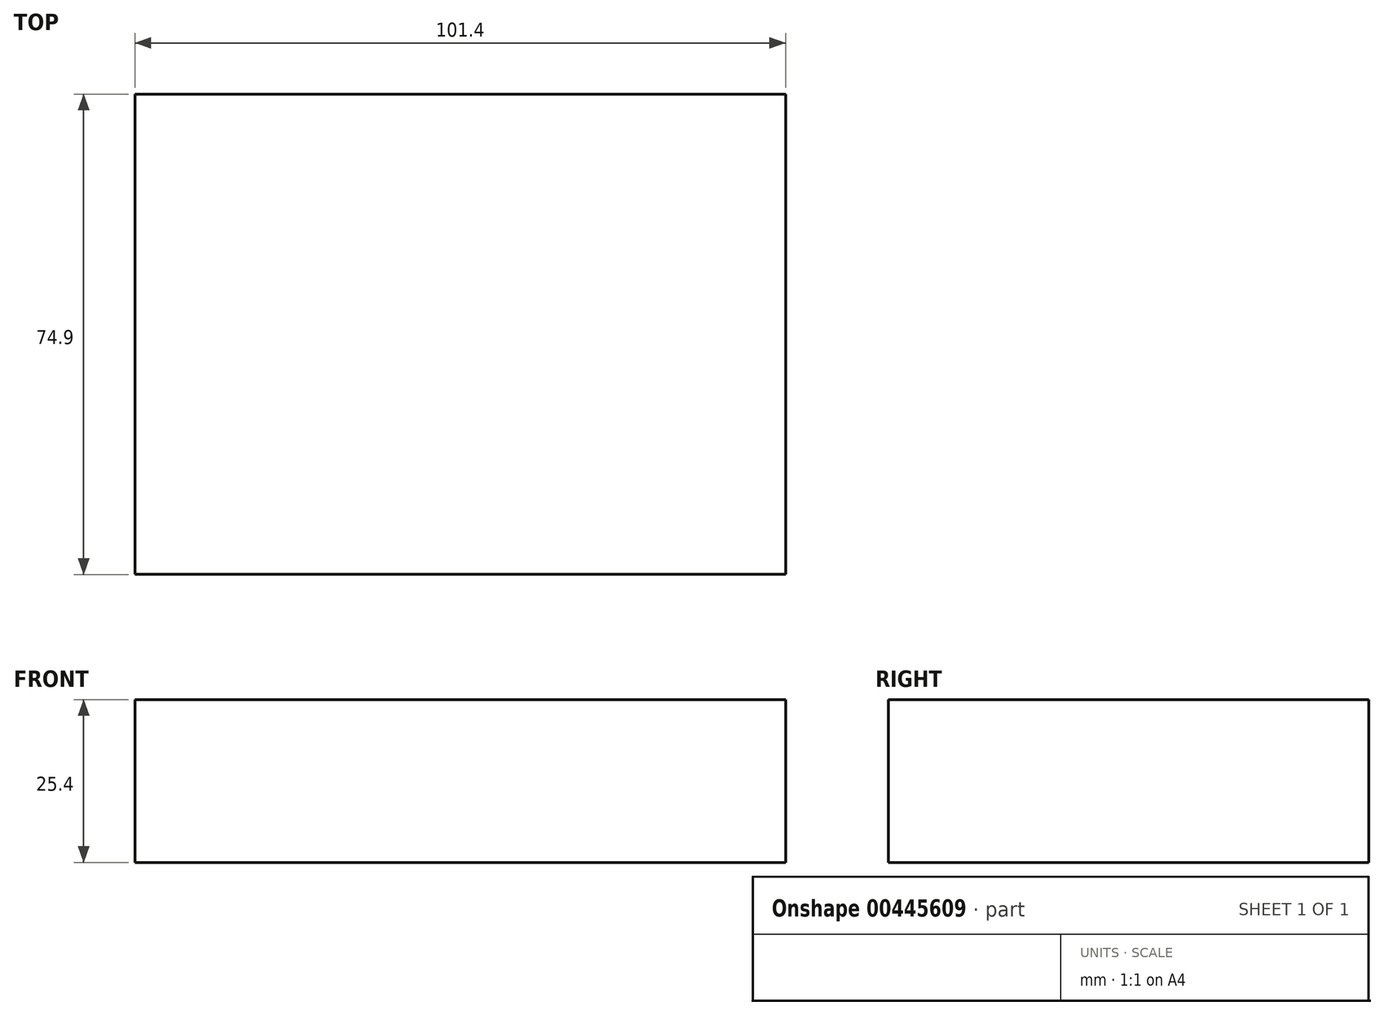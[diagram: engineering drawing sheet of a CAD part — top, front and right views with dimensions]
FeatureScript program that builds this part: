
annotation { "Feature Type Name" : "Feature", "Feature Type Description" : "" }
export const myFeature = defineFeature(function(context is Context, id is Id, definition is map)
    precondition{}
    {
        {
            var Q0;
            Q0=qCreatedBy(makeId("Top.planeOp"),FACE);
            var sketch = newSketch(context, id + "F0", { "sketchPlane" : qUnion([Q0])});
            skLineSegment(sketch, "E0.bottom", {"start": v(50.7, 37.45) * mm, "end": v(-50.7, 37.45) * mm});
            skLineSegment(sketch, "E0.top", {"start": v(50.7, -37.45) * mm, "end": v(-50.7, -37.45) * mm});
            skLineSegment(sketch, "E0.left", {"start": v(50.7, 37.45) * mm, "end": v(50.7, -37.45) * mm});
            skLineSegment(sketch, "E0.right", {"start": v(-50.7, 37.45) * mm, "end": v(-50.7, -37.45) * mm});
            skPoint(sketch, "E0.middle", {"position": v(0, 0) * mm});
            skSolve(sketch);
        }
        {
            var Q0;
            Q0=makeQuery(id+"F0.imprint","IMPRINT",FACE,{"disambiguationData":[TD([[makeQuery(id+"F0.imprint","IMPRINT",EDGE,{"derivedFrom":sQuery(id+"F0.wireOp",EDGE,"E0.bottom")}),1.0]])]});
            extrude(context, id + "F1", {"entities" : qUnion([Q0]), "depth" : 25.4 * mm});
        }
    });
